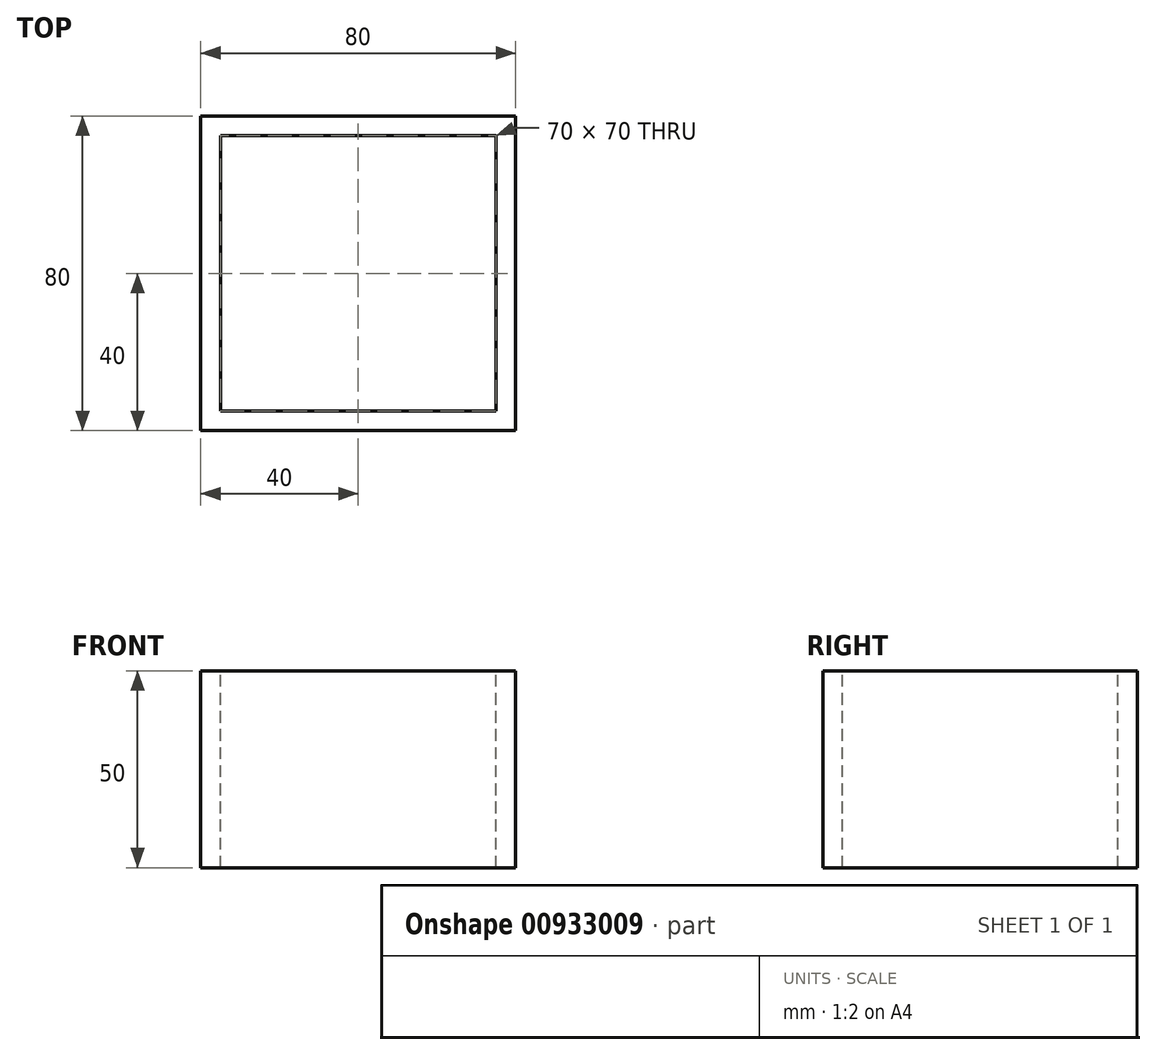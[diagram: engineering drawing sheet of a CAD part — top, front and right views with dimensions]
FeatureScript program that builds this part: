
annotation { "Feature Type Name" : "Feature", "Feature Type Description" : "" }
export const myFeature = defineFeature(function(context is Context, id is Id, definition is map)
    precondition{}
    {
        {
            var Q0;
            Q0=qCreatedBy(makeId("Top.planeOp"),FACE);
            var sketch = newSketch(context, id + "F0", { "sketchPlane" : qUnion([Q0])});
            skLineSegment(sketch, "E0.bottom", {"start": v(0, 0) * mm, "end": v(80, 0) * mm});
            skLineSegment(sketch, "E0.top", {"start": v(0, 80) * mm, "end": v(80, 80) * mm});
            skLineSegment(sketch, "E0.left", {"start": v(0, 0) * mm, "end": v(0, 80) * mm});
            skLineSegment(sketch, "E0.right", {"start": v(80, 0) * mm, "end": v(80, 80) * mm});
            skSolve(sketch);
        }
        {
            var Q0;
            Q0=makeQuery(id+"F0.imprint","IMPRINT",FACE,{"disambiguationData":[TD([[makeQuery(id+"F0.imprint","IMPRINT",EDGE,{"derivedFrom":sQuery(id+"F0.wireOp",EDGE,"E0.bottom")}),1.0]])]});
            extrude(context, id + "F1", {"entities" : qUnion([Q0]), "depth" : 50 * mm, "offsetDistance" : 25 * mm});
        }
        {
            var Q0;
            Q0=makeQuery(id+"F1.opExtrude","CAP_FACE",FACE,{"disambiguationData":[OSD([sQuery(id+"F0.wireOp",EDGE,"E0.bottom"),sQuery(id+"F0.wireOp",EDGE,"E0.top"),sQuery(id+"F0.wireOp",EDGE,"E0.left"),sQuery(id+"F0.wireOp",EDGE,"E0.right")])],"isStart":false});
            var sketch = newSketch(context, id + "F2", { "sketchPlane" : qUnion([Q0])});
            skLineSegment(sketch, "E1.bottom", {"start": v(5, 5) * mm, "end": v(75, 5) * mm});
            skLineSegment(sketch, "E1.top", {"start": v(5, 75) * mm, "end": v(75, 75) * mm});
            skLineSegment(sketch, "E1.left", {"start": v(5, 5) * mm, "end": v(5, 75) * mm});
            skLineSegment(sketch, "E1.right", {"start": v(75, 5) * mm, "end": v(75, 75) * mm});
            skSolve(sketch);
        }
        {
            var Q0;
            Q0=makeQuery(id+"F2.imprint","IMPRINT",FACE,{"disambiguationData":[TD([[makeQuery(id+"F2.imprint","IMPRINT",EDGE,{"derivedFrom":sQuery(id+"F2.wireOp",EDGE,"E1.bottom")}),1.0]])]});
            extrude(context, id + "F3", {"entities" : qUnion([Q0]), "operationType" : NewBodyOperationType.REMOVE, "oppositeDirection" : true, "depth" : 40 * mm, "offsetDistance" : 25 * mm});
        }
        {
            var Q0;
            Q0=makeQuery(id+"F2.imprint","IMPRINT",FACE,{"disambiguationData":[TD([[makeQuery(id+"F2.imprint","IMPRINT",EDGE,{"derivedFrom":sQuery(id+"F2.wireOp",EDGE,"E1.bottom")}),1.0]])]});
            extrude(context, id + "F4", {"entities" : qUnion([Q0]), "operationType" : NewBodyOperationType.REMOVE, "endBound" : BoundingType.THROUGH_ALL, "oppositeDirection" : true, "depth" : 33.2 * mm, "offsetDistance" : 25 * mm});
        }
    });
